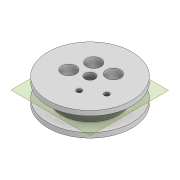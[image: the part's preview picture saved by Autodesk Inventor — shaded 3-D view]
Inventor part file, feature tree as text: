
AUTODESK INVENTOR PART (.ipt)
format: ipt  version: 2022 (Build 260153000, 153)  size: 249,344 bytes
history: native  units: mm
features: extrude x7, sketch x6, plane x3, pattern_circular x1, fillet x1, mirror x1, projected_geometry x1
ambient origin geometry x8: Origin, YZ Plane, XZ Plane, XY Plane, X Axis, Y Axis, Z Axis, Center Point
bodies: Solid1 (feature_tree)
feature tree (20):
  extrude  "Extrusion1"  Depth=24.0mm
  extrude  "Extrusion2"  Depth=6.0mm TaperAngle=0.0deg
  pattern_circular  "Circular Pattern1"  Count=5 Angle=360.0deg
  plane  "Work Plane1"
  plane  "Work Plane2"
  extrude  "Extrusion3"  [1 undecoded]
  extrude  "Extrusion4"  Depth=10.0mm
  fillet  "Fillet1"  Radius=2.5mm
  plane  "Work Plane3"
  extrude  "Extrusion5"  Depth=10.0mm
  mirror  "Mirror1"
  sketch  "Sketch6"  dims[d13=9.599311mm d14=-9.599311mm d15=2.5mm d16=2.5mm d17=1.7mm d18=7.0mm d19=0.0mm d20=2.5mm d21=2.5mm d22=1.7mm d23=7.0mm d24=0.0mm d25=1.0mm d26=35.0mm d27=2.0mm d28=0.0mm d29=2.1mm d30=10.0mm d31=3.0mm d32=2.1mm d35=10.0mm d36=0.0mm d37=100.0mm d38=0.0mm d39=3.0mm d40=7.5mm]
  extrude  "Extrusion6"  Depth=10.0mm TaperAngle=0.0deg
  extrude  "Extrusion7"  Depth=10.0mm
  sketch  "Sketch1"  dims[d0=4.2mm d2=24.0mm]
  sketch  "Sketch2"  dims[d3=4.0mm d4=6.0mm d5=0.0mm]
  sketch  "Sketch3"  dims[d6=6.0mm]
  sketch  "Sketch4"  dims[d7=7.0mm]
  sketch  "Sketch5"  dims[d8=10.0mm d9=0.0mm d10=50.0mm d11=360.0deg]
  projected_geometry  "Projected Loop1"
note: 1 required parameter value undecoded (feature->parameter linkage not recoverable at this tier; creation-order binding heuristic only, values carry confidence <= 0.55)
